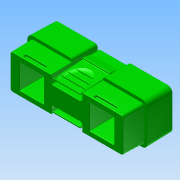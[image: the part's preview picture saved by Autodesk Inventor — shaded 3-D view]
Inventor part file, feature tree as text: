
AUTODESK INVENTOR PART (.ipt)
format: ipt  version: 2015 (Build 190159000, 159)  size: 1,799,680 bytes
history: native  units: in
note: dims shown in document units (in); Inventor stores cm internally (conversion verified against a paired STEP export)
features: extrude x8, fillet x8, sketch x7, draft x4, mirror x2, projected_geometry x1
ambient origin geometry x8: Origin, YZ Plane, XZ Plane, XY Plane, X Axis, Y Axis, Z Axis, Center Point
bodies: Solid1 (feature_tree)
feature tree (30):
  sketch  "Sketch1"  dims[d0=0.34in d1=0.8in]
  extrude  "Extrusion1"  Depth=0.8in
  extrude  "Extrusion2"  Depth=0.2975in
  extrude  "Extrusion3"  Depth=0.06in
  draft  "FaceDraft1"
  draft  "FaceDraft2"
  extrude  "Extrusion4"  Depth=0.5in TaperAngle=0.0deg
  extrude  "Extrusion5"  Depth=0.15in
  fillet  "Fillet1"  Radius=0.33in
  fillet  "Fillet2"  Radius=0.0069in
  extrude  "Extrusion6"  Depth=0.17in
  draft  "FaceDraft3"
  fillet  "Fillet3"  Radius=0.17in
  fillet  "Fillet4"  Radius=0.04in
  fillet  "Fillet5"  Radius=0.09in
  extrude  "Extrusion7"  Depth=0.03in
  extrude  "Extrusion8"  Depth=0.33in
  draft  "FaceDraft4"
  fillet  "Fillet6"  Radius=0.0206in
  fillet  "Fillet7"  Radius=0.0412in
  fillet  "Fillet8"  Radius=0.2625in
  mirror  "Mirror1"
  mirror  "Mirror2"
  sketch  "Sketch2"  dims[d2=0.175in d3=0.2975in]
  sketch  "Sketch3"  dims[d4=0.06in d5=0.06in]
  sketch  "Sketch4"  dims[d6=0.4in d7=0.0in d8=0.5in d9=0.0in]
  projected_geometry  "Projected Loop1"
  sketch  "Sketch5"  dims[d11=0.8in d12=0.15in d13=0.33in d14=0.0in d15=0.0069in]
  sketch  "Sketch6"  dims[d16=0.0069in d17=0.17in d18=0.17in d19=0.04in d20=0.09in]
  sketch  "Sketch7"  dims[d21=0.84in d22=0.03in d24=0.33in d25=0.0206in d26=0.0412in d27=0.2625in d28=0.0in d31=0.25in d32=0.1in d33=0.2in d34=0.6174in d35=0.01in d36=0.02in d37=0.0in d38=0.05in d39=0.185in d40=0.02in d41=0.125in d42=0.24in d43=0.36in d44=0.26in d45=0.01in d46=0.01in d47=0.0in d48=0.0137in d49=0.4in d50=0.06in d51=0.48in d52=0.3in d53=0.04in d54=0.0in d55=0.2375in d56=0.47in d57=0.186in d58=0.47in d59=0.0in d60=0.0069in d61=0.05in d62=0.01in d63=0.005in d64=0.1in]
